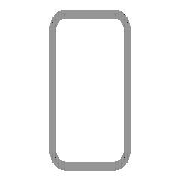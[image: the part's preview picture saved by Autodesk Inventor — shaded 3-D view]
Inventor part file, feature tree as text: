
AUTODESK INVENTOR PART (.ipt)
format: ipt  version: 2025 (Build 290162010, 162A)  size: 136,192 bytes
history: native  units: mm (DEFAULTED — no unit token found)
features: other x4, sketch x1, plane x1
ambient origin geometry x8: Origin, YZ Plane, XZ Plane, XY Plane, X Axis, Y Axis, Z Axis, Center Point
bodies: Solid1 (feature_tree), Body (feature_tree)
feature tree (6):
  parser-record x1  (decoder bookkeeping rows leaked as tree rows — omitted from the tree; the rows remain in map.json)
  other  "Driven Length"
  other  "Start Plane"
  other  "End Plane"
  sketch  "Sketch3"  dims[d3=3000.0mm d4=0.0mm d7=3.75mm d10=60.0mm d11=40.0mm d12=2.5mm d13=-0.0mm d14=3000.0mm d15=30.0mm d16=20.0mm d17=90.0deg d18=3000.0mm]
  plane  "Work Plane3"
